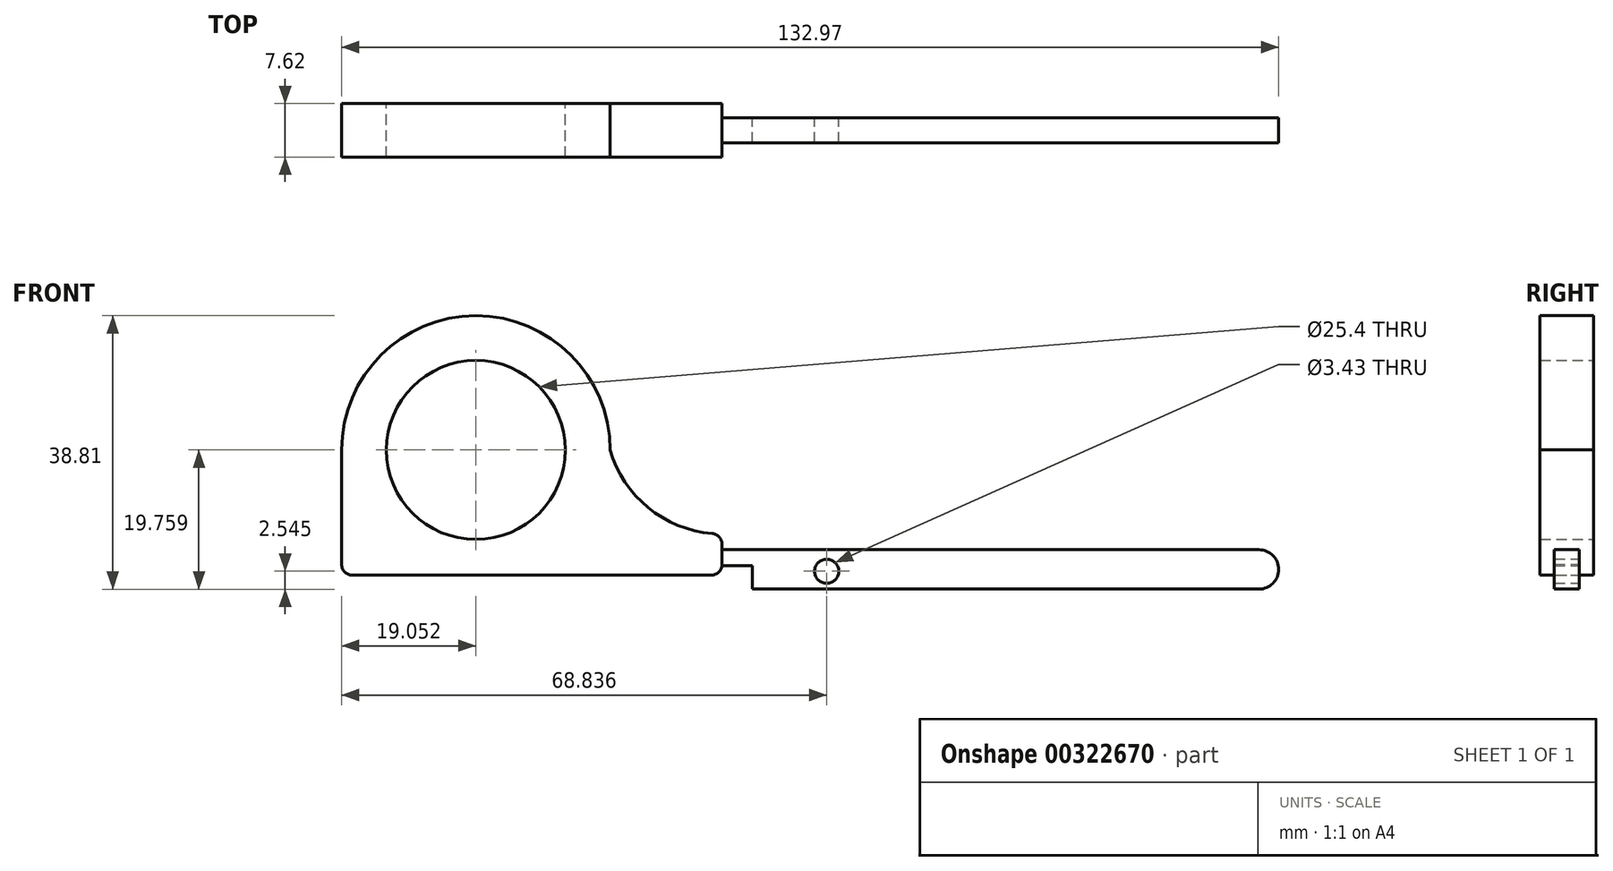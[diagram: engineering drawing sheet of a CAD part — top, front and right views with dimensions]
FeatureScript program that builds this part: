
annotation { "Feature Type Name" : "Feature", "Feature Type Description" : "" }
export const myFeature = defineFeature(function(context is Context, id is Id, definition is map)
    precondition{}
    {
        {
            var Q0;
            Q0=qCreatedBy(makeId("Front.planeOp"),FACE);
            var sketch = newSketch(context, id + "F0", { "sketchPlane" : qUnion([Q0])});
            skLineSegment(sketch, "E0", {"start": v(-41.74, 12.46) * mm, "end": v(-41.74, -3.8) * mm});
            skLineSegment(sketch, "E1", {"start": v(-40.21, -5.32) * mm, "end": v(10.71, -5.32) * mm});
            skLineSegment(sketch, "E2", {"start": v(12.24, -3.8) * mm, "end": v(12.24, -0.91) * mm});
            skArc(sketch, "E3", {"start": v(-3.64, 12.46) * mm, "mid": v(1.76, 4.28) * mm, "end": v(10.84, 0.6) * mm});
            skArc(sketch, "E4", {"start": v(-3.64, 12.46) * mm, "mid": v(-22.69, 31.5) * mm, "end": v(-41.74, 12.46) * mm});
            skCircle(sketch, "E5", {"center": v(-22.69, 12.46) * mm, "radius": 12.7 * mm});
            skPoint(sketch, "E6.visualSharp", {"position": v(-41.74, -5.32) * mm});
            skArc(sketch, "E6.filletArc", {"start": v(-41.74, -3.8) * mm, "mid": v(-41.3, -4.87) * mm, "end": v(-40.21, -5.32) * mm});
            skPoint(sketch, "E7.visualSharp", {"position": v(12.24, -5.32) * mm});
            skArc(sketch, "E7.filletArc", {"start": v(10.71, -5.32) * mm, "mid": v(11.8, -4.87) * mm, "end": v(12.24, -3.8) * mm});
            skPoint(sketch, "E8.visualSharp", {"position": v(12.24, 0.55) * mm});
            skArc(sketch, "E8.filletArc", {"start": v(12.24, -0.91) * mm, "mid": v(11.83, 0.12) * mm, "end": v(10.84, 0.6) * mm});
            skPoint(sketch, "E9.endSnap0", {"position": v(12.24, -2.36) * mm});
            skLineSegment(sketch, "E10", {"start": v(12.24, -1.7) * mm, "end": v(88.44, -1.7) * mm});
            skLineSegment(sketch, "E11", {"start": v(12.24, -4) * mm, "end": v(16.55, -4) * mm});
            skLineSegment(sketch, "E12", {"start": v(16.55, -4) * mm, "end": v(16.55, -7.3) * mm});
            skLineSegment(sketch, "E13", {"start": v(16.55, -7.3) * mm, "end": v(88.44, -7.3) * mm});
            skCircle(sketch, "E14", {"center": v(27.1, -4.76) * mm, "radius": 1.71 * mm});
            skArc(sketch, "E15", {"start": v(88.44, -7.3) * mm, "mid": v(91.23, -4.5) * mm, "end": v(88.44, -1.7) * mm});
            skLineSegment(sketch, "E16", {"start": v(12.24, -1.7) * mm, "end": v(12.24, -4) * mm});
            skSolve(sketch);
        }
        {
            var Q0;
            Q0=makeQuery(id+"F0.imprint","IMPRINT",FACE,{"disambiguationData":[TD([[makeQuery(id+"F0.imprint","IMPRINT",EDGE,{"derivedFrom":sQuery(id+"F0.wireOp",EDGE,"E0")}),1.0]])]});
            extrude(context, id + "F1", {"entities" : qUnion([Q0]), "depth" : 7.62 * mm, "symmetric" : true});
        }
        {
            var Q0;
            {var subQ1=sQuery(id+"F0.wireOp",EDGE,"E10");Q0=makeQuery(id+"F0.imprint","IMPRINT",FACE,{"disambiguationData":[TD([[makeQuery(id+"F0.imprint","IMPRINT",EDGE,{"derivedFrom":subQ1}),-1.0]])]});}
            extrude(context, id + "F2", {"entities" : qUnion([Q0]), "operationType" : NewBodyOperationType.ADD, "depth" : 3.56 * mm, "symmetric" : true});
        }
    });
